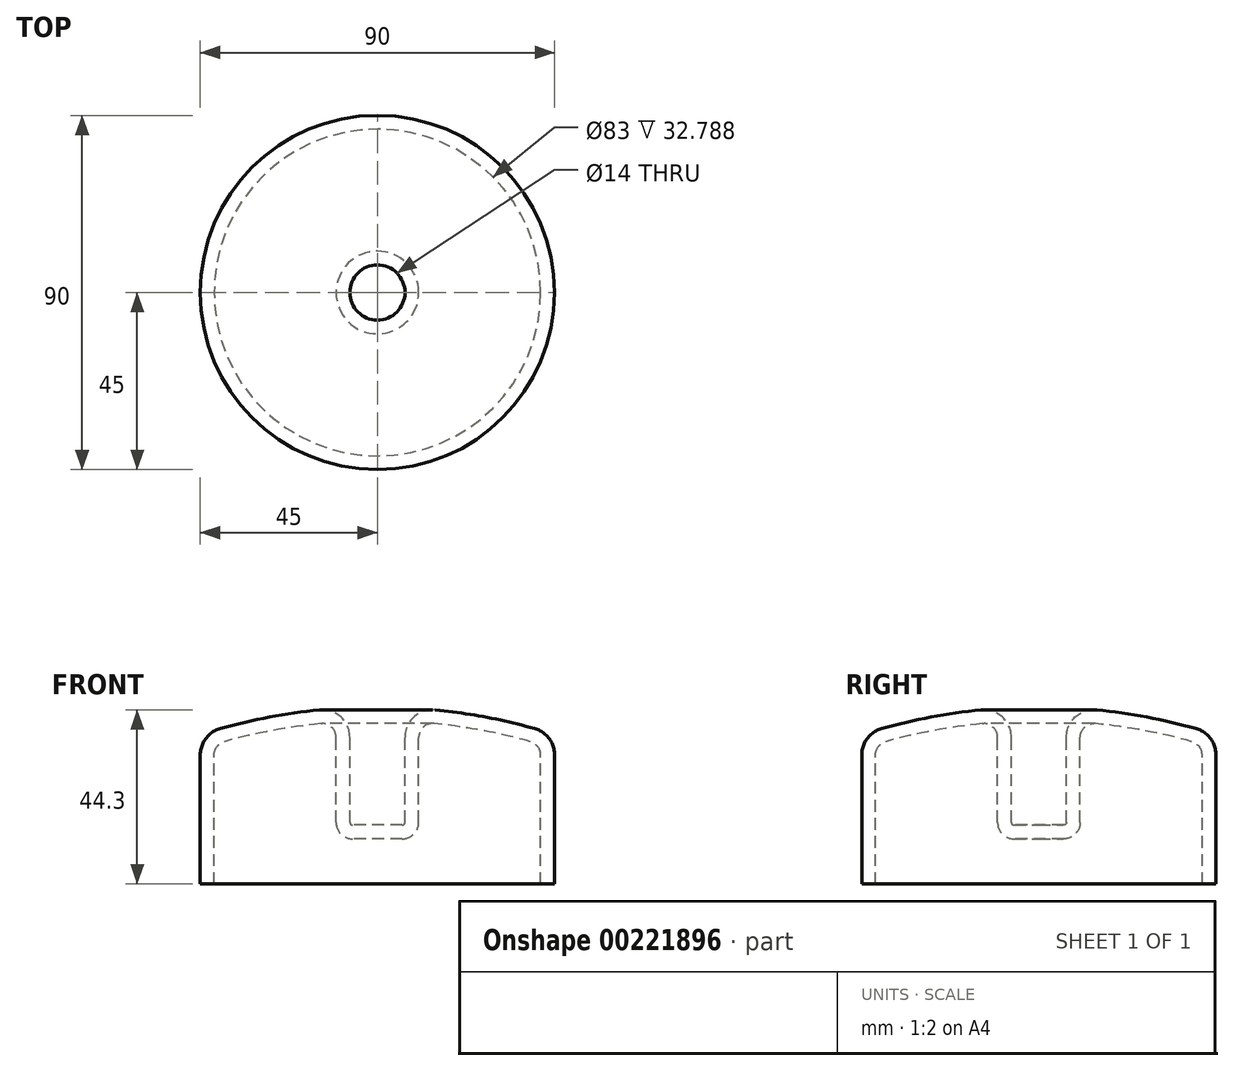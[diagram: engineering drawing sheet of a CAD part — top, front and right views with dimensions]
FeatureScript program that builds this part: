
annotation { "Feature Type Name" : "Feature", "Feature Type Description" : "" }
export const myFeature = defineFeature(function(context is Context, id is Id, definition is map)
    precondition{}
    {
        {
            var Q0;
            Q0=qCreatedBy(makeId("Front.planeOp"),FACE);
            var sketch = newSketch(context, id + "F0", { "sketchPlane" : qUnion([Q0])});
            skLineSegment(sketch, "E0", {"start": v(-6.3, 15) * mm, "end": v(0, 15) * mm});
            skLineSegment(sketch, "E1", {"start": v(-7, 15.7) * mm, "end": v(-7, 37.3) * mm});
            skArc(sketch, "E2.trimOffspring", {"start": v(-14.7, 44.27) * mm, "mid": v(-27.4, 42.45) * mm, "end": v(-39.88, 39.53) * mm});
            skArc(sketch, "E3.filletArc", {"start": v(-39.88, 39.53) * mm, "mid": v(-43.58, 37.02) * mm, "end": v(-45, 32.79) * mm});
            skArc(sketch, "E4.filletArc", {"start": v(-7, 37.3) * mm, "mid": v(-9.3, 42.5) * mm, "end": v(-14.7, 44.27) * mm});
            skArc(sketch, "E5.filletArc", {"start": v(-7, 15.7) * mm, "mid": v(-6.8, 15.2) * mm, "end": v(-6.3, 15) * mm});
            skLineSegment(sketch, "E6", {"start": v(-45, 32.79) * mm, "end": v(-45, 0) * mm});
            skLineSegment(sketch, "E7.0", {"start": v(-41.5, 32.79) * mm, "end": v(-41.5, 0) * mm});
            skArc(sketch, "E7.1", {"start": v(-38.94, 36.16) * mm, "mid": v(-40.79, 34.9) * mm, "end": v(-41.5, 32.79) * mm});
            skArc(sketch, "E7.2", {"start": v(-14.35, 40.79) * mm, "mid": v(-26.75, 39) * mm, "end": v(-38.94, 36.16) * mm});
            skLineSegment(sketch, "E7.3", {"start": v(-6.3, 11.5) * mm, "end": v(0, 11.5) * mm});
            skArc(sketch, "E7.4", {"start": v(-10.5, 15.7) * mm, "mid": v(-9.27, 12.73) * mm, "end": v(-6.3, 11.5) * mm});
            skLineSegment(sketch, "E7.5", {"start": v(-10.5, 15.7) * mm, "end": v(-10.5, 37.3) * mm});
            skArc(sketch, "E7.6", {"start": v(-10.5, 37.3) * mm, "mid": v(-11.65, 39.9) * mm, "end": v(-14.35, 40.79) * mm});
            skLineSegment(sketch, "E8", {"start": v(-45, 0) * mm, "end": v(-41.5, 0) * mm});
            skLineSegment(sketch, "E9", {"start": v(0, 15) * mm, "end": v(0, 11.5) * mm});
            skSolve(sketch);
        }
        {
            var Q0;
            Q0 = qSketchRegion(id + "F0", true);
            var Q1;
            Q1=sQuery(id+"F0.wireOp",EDGE,"E9");
            revolve(context, id + "F1", {"entities" : qUnion([Q0]), "axis" : qUnion([Q1]), "revolveType" : RevolveType.FULL});
        }
    });
